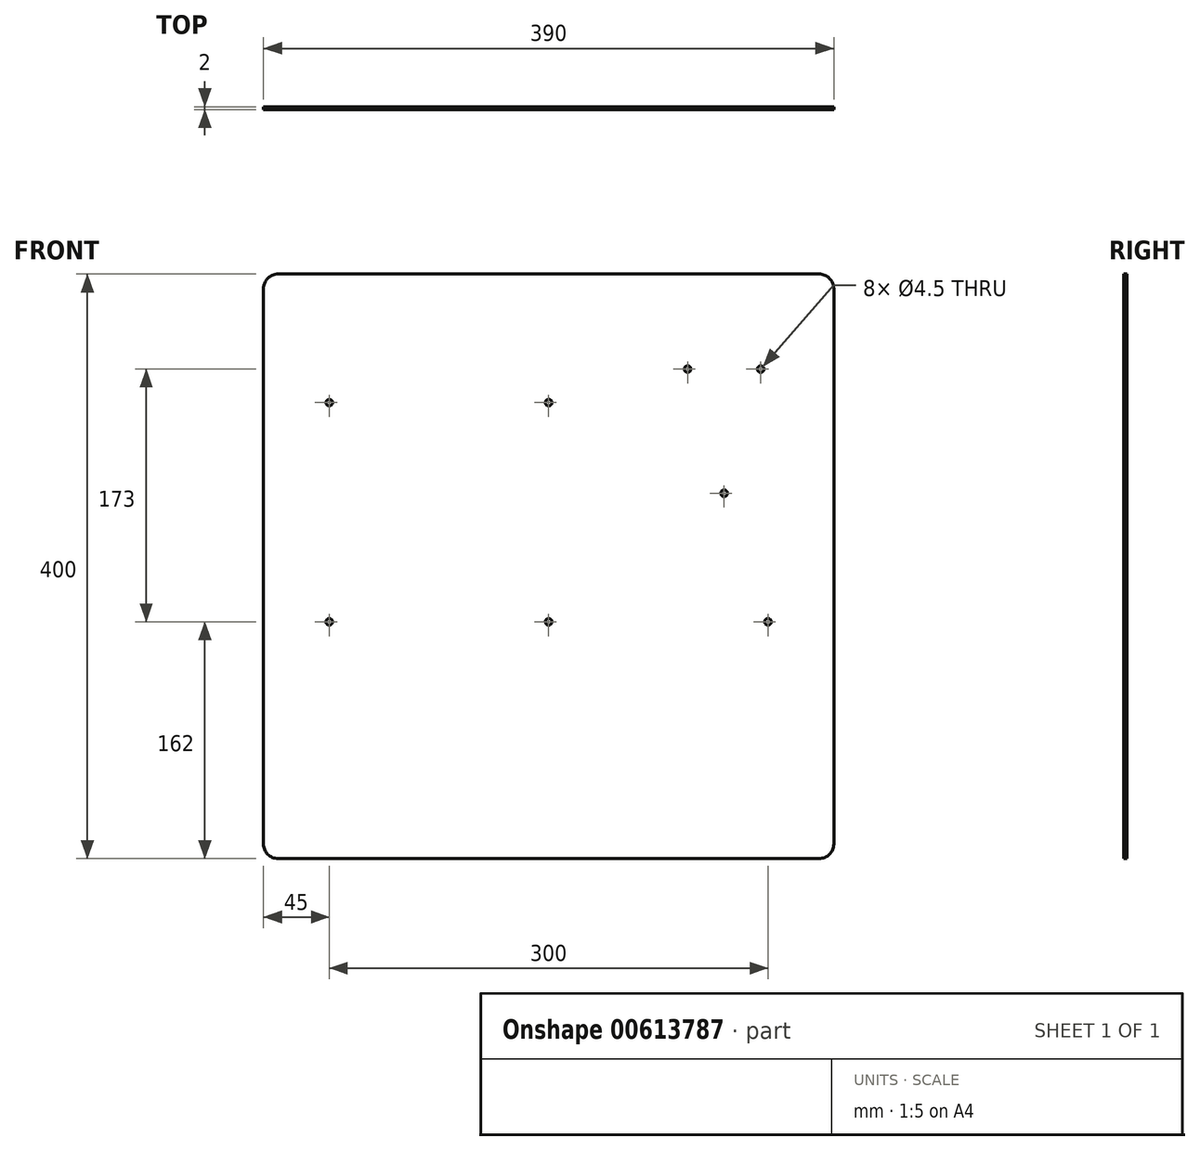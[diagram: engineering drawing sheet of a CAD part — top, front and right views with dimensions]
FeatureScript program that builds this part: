
annotation { "Feature Type Name" : "Feature", "Feature Type Description" : "" }
export const myFeature = defineFeature(function(context is Context, id is Id, definition is map)
    precondition{}
    {
        {
            var Q0;
            Q0=qCreatedBy(makeId("Front.planeOp"),FACE);
            var sketch = newSketch(context, id + "F0", { "sketchPlane" : qUnion([Q0])});
            skLineSegment(sketch, "E0.bottom", {"start": v(-195, 0) * mm, "end": v(195, 0) * mm});
            skLineSegment(sketch, "E0.top", {"start": v(-195, 400) * mm, "end": v(195, 400) * mm});
            skLineSegment(sketch, "E0.left", {"start": v(-195, 0) * mm, "end": v(-195, 400) * mm});
            skLineSegment(sketch, "E0.right", {"start": v(195, 0) * mm, "end": v(195, 400) * mm});
            skSolve(sketch);
        }
        {
            var Q0;
            Q0=makeQuery(id+"F0.imprint","IMPRINT",FACE,{"disambiguationData":[TD([[makeQuery(id+"F0.imprint","IMPRINT",EDGE,{"derivedFrom":sQuery(id+"F0.wireOp",EDGE,"E0.bottom")}),1.0]])]});
            extrude(context, id + "F1", {"entities" : qUnion([Q0]), "depth" : 2 * mm, "offsetDistance" : 25 * mm});
        }
        {
            var Q0;
            Q0=makeQuery(id+"F1.opExtrude","CAP_FACE",FACE,{"disambiguationData":[OSD([sQuery(id+"F0.wireOp",EDGE,"E0.bottom"),sQuery(id+"F0.wireOp",EDGE,"E0.top"),sQuery(id+"F0.wireOp",EDGE,"E0.left"),sQuery(id+"F0.wireOp",EDGE,"E0.right")])],"isStart":false});
            var sketch = newSketch(context, id + "F2", { "sketchPlane" : qUnion([Q0])});
            skCircle(sketch, "E1", {"center": v(145, 335) * mm, "radius": 2.25 * mm});
            skLineSegment(sketch, "E2", {"start": v(145, 335) * mm, "end": v(95, 335) * mm, "construction": true});
            skLineSegment(sketch, "E3", {"start": v(120, 335) * mm, "end": v(120, 250) * mm, "construction": true});
            skCircle(sketch, "E4", {"center": v(95, 335) * mm, "radius": 2.25 * mm});
            skCircle(sketch, "E5", {"center": v(120, 250) * mm, "radius": 2.25 * mm});
            skLineSegment(sketch, "E6", {"start": v(-150, 162) * mm, "end": v(150, 162) * mm, "construction": true});
            skLineSegment(sketch, "E7", {"start": v(0, 0) * mm, "end": v(0, 445.27) * mm, "construction": true});
            skPoint(sketch, "E7.endSnap0", {"position": v(0, 162) * mm});
            skCircle(sketch, "E8", {"center": v(0, 162) * mm, "radius": 2.25 * mm});
            skCircle(sketch, "E9", {"center": v(-150, 162) * mm, "radius": 2.25 * mm});
            skCircle(sketch, "E10", {"center": v(150, 162) * mm, "radius": 2.25 * mm});
            skLineSegment(sketch, "E11", {"start": v(0, 312) * mm, "end": v(-254.9, 312) * mm, "construction": true});
            skLineSegment(sketch, "E12", {"start": v(-150, 162) * mm, "end": v(-150, 331.48) * mm, "construction": true});
            skCircle(sketch, "E13", {"center": v(-150, 312) * mm, "radius": 2.25 * mm});
            skCircle(sketch, "E14", {"center": v(0, 312) * mm, "radius": 2.25 * mm});
            skSolve(sketch);
        }
        {
            var Q0;
            Q0 = qSketchRegion(id + "F2", true);
            extrude(context, id + "F3", {"entities" : qUnion([Q0]), "operationType" : NewBodyOperationType.REMOVE, "oppositeDirection" : true, "depth" : 25 * mm, "offsetDistance" : 25 * mm});
        }
        {
            var Q0;
            Q0=makeQuery(id+"F1.opExtrude","SWEPT_EDGE",EDGE,{"disambiguationData":[OSD([sQuery(id+"F0.wireOp",EDGE,"E0.top"),sQuery(id+"F0.wireOp",EDGE,"E0.right")])]});
            var Q1;
            Q1=makeQuery(id+"F1.opExtrude","SWEPT_EDGE",EDGE,{"disambiguationData":[OSD([sQuery(id+"F0.wireOp",EDGE,"E0.top"),sQuery(id+"F0.wireOp",EDGE,"E0.left")])]});
            var Q2;
            Q2=makeQuery(id+"F1.opExtrude","SWEPT_EDGE",EDGE,{"disambiguationData":[OSD([sQuery(id+"F0.wireOp",EDGE,"E0.bottom"),sQuery(id+"F0.wireOp",EDGE,"E0.right")])]});
            var Q3;
            Q3=makeQuery(id+"F1.opExtrude","SWEPT_EDGE",EDGE,{"disambiguationData":[OSD([sQuery(id+"F0.wireOp",EDGE,"E0.bottom"),sQuery(id+"F0.wireOp",EDGE,"E0.left")])]});
            fillet(context, id + "F4", {"entities" : qUnion([Q0, Q1, Q2, Q3]), "radius" : 10 * mm, "tangentPropagation" : true, "allowEdgeOverflow" : false});
        }
    });
